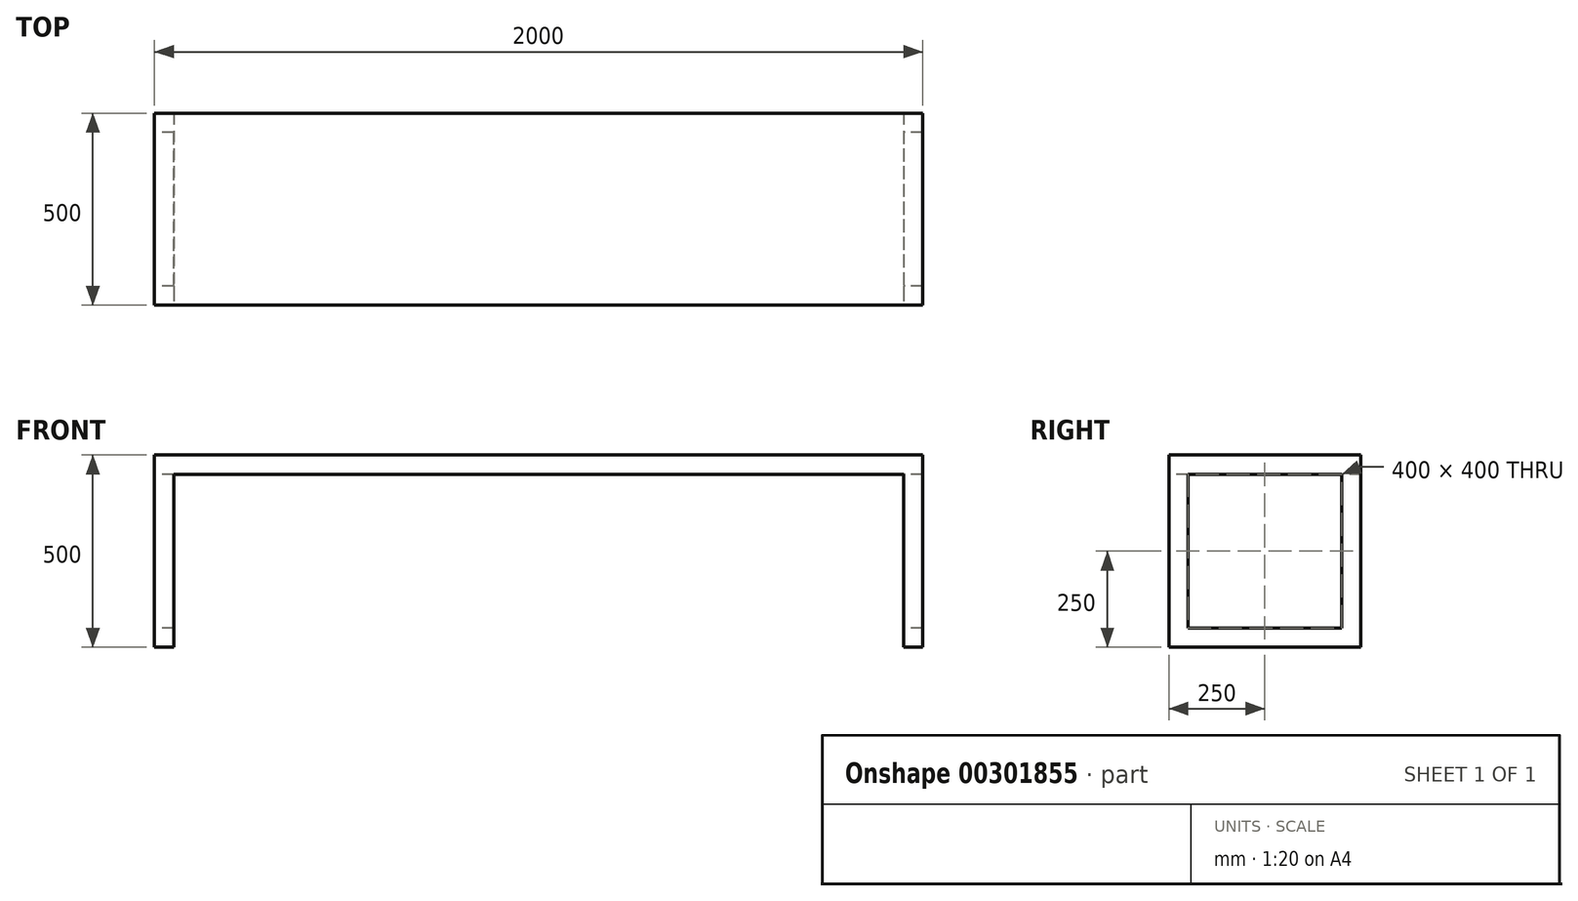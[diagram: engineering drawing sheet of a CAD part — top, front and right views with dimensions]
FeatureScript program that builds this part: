
annotation { "Feature Type Name" : "Feature", "Feature Type Description" : "" }
export const myFeature = defineFeature(function(context is Context, id is Id, definition is map)
    precondition{}
    {
        {
            var Q0;
            Q0=qCreatedBy(makeId("Front.planeOp"),FACE);
            var sketch = newSketch(context, id + "F0", { "sketchPlane" : qUnion([Q0])});
            skLineSegment(sketch, "E0.bottom", {"start": v(0, 0) * mm, "end": v(2000, 0) * mm});
            skLineSegment(sketch, "E0.top", {"start": v(0, 500) * mm, "end": v(2000, 500) * mm});
            skLineSegment(sketch, "E0.left", {"start": v(0, 0) * mm, "end": v(0, 500) * mm});
            skLineSegment(sketch, "E0.right", {"start": v(2000, 0) * mm, "end": v(2000, 500) * mm});
            skSolve(sketch);
        }
        {
            var Q0;
            Q0=makeQuery(id+"F0.imprint","IMPRINT",FACE,{"disambiguationData":[TD([[makeQuery(id+"F0.imprint","IMPRINT",EDGE,{"derivedFrom":sQuery(id+"F0.wireOp",EDGE,"E0.bottom")}),1.0]])]});
            extrude(context, id + "F1", {"entities" : qUnion([Q0]), "depth" : 500 * mm});
        }
        {
            var Q0;
            Q0=makeQuery(id+"F1.opExtrude","CAP_FACE",FACE,{"disambiguationData":[OSD([sQuery(id+"F0.wireOp",EDGE,"E0.bottom"),sQuery(id+"F0.wireOp",EDGE,"E0.top"),sQuery(id+"F0.wireOp",EDGE,"E0.left"),sQuery(id+"F0.wireOp",EDGE,"E0.right")])],"isStart":false});
            var sketch = newSketch(context, id + "F2", { "sketchPlane" : qUnion([Q0])});
            skLineSegment(sketch, "E1", {"start": v(50, 0) * mm, "end": v(50, 450) * mm});
            skLineSegment(sketch, "E2", {"start": v(50, 450) * mm, "end": v(1950, 450) * mm});
            skLineSegment(sketch, "E3", {"start": v(1950, 450) * mm, "end": v(1950, 0) * mm});
            skSolve(sketch);
        }
        {
            var Q0;
            {var subQ0=sQuery(id+"F2.wireOp",EDGE,"E1");Q0=makeQuery(id+"F2.imprint","IMPRINT",FACE,{"disambiguationData":[TD([[makeQuery(id+"F2.imprint","IMPRINT",EDGE,{"derivedFrom":subQ0}),-1.0]])]});}
            extrude(context, id + "F3", {"entities" : qUnion([Q0]), "operationType" : NewBodyOperationType.REMOVE, "endBound" : BoundingType.THROUGH_ALL, "oppositeDirection" : true, "depth" : 25 * mm});
        }
        {
            var Q0;
            Q0=makeQuery(id+"F1.opExtrude","SWEPT_FACE",FACE,{"disambiguationData":[OSD([sQuery(id+"F0.wireOp",EDGE,"E0.left")])]});
            var sketch = newSketch(context, id + "F4", { "sketchPlane" : qUnion([Q0])});
            skLineSegment(sketch, "E4.bottom", {"start": v(50, 450) * mm, "end": v(450, 450) * mm});
            skLineSegment(sketch, "E4.top", {"start": v(50, 50) * mm, "end": v(450, 50) * mm});
            skLineSegment(sketch, "E4.left", {"start": v(50, 450) * mm, "end": v(50, 50) * mm});
            skLineSegment(sketch, "E4.right", {"start": v(450, 450) * mm, "end": v(450, 50) * mm});
            skSolve(sketch);
        }
        {
            var Q0;
            Q0=makeQuery(id+"F4.imprint","IMPRINT",FACE,{"disambiguationData":[TD([[makeQuery(id+"F4.imprint","IMPRINT",EDGE,{"derivedFrom":sQuery(id+"F4.wireOp",EDGE,"E4.bottom")}),-1.0]])]});
            extrude(context, id + "F5", {"entities" : qUnion([Q0]), "operationType" : NewBodyOperationType.REMOVE, "endBound" : BoundingType.THROUGH_ALL, "oppositeDirection" : true, "depth" : 25 * mm});
        }
    });
